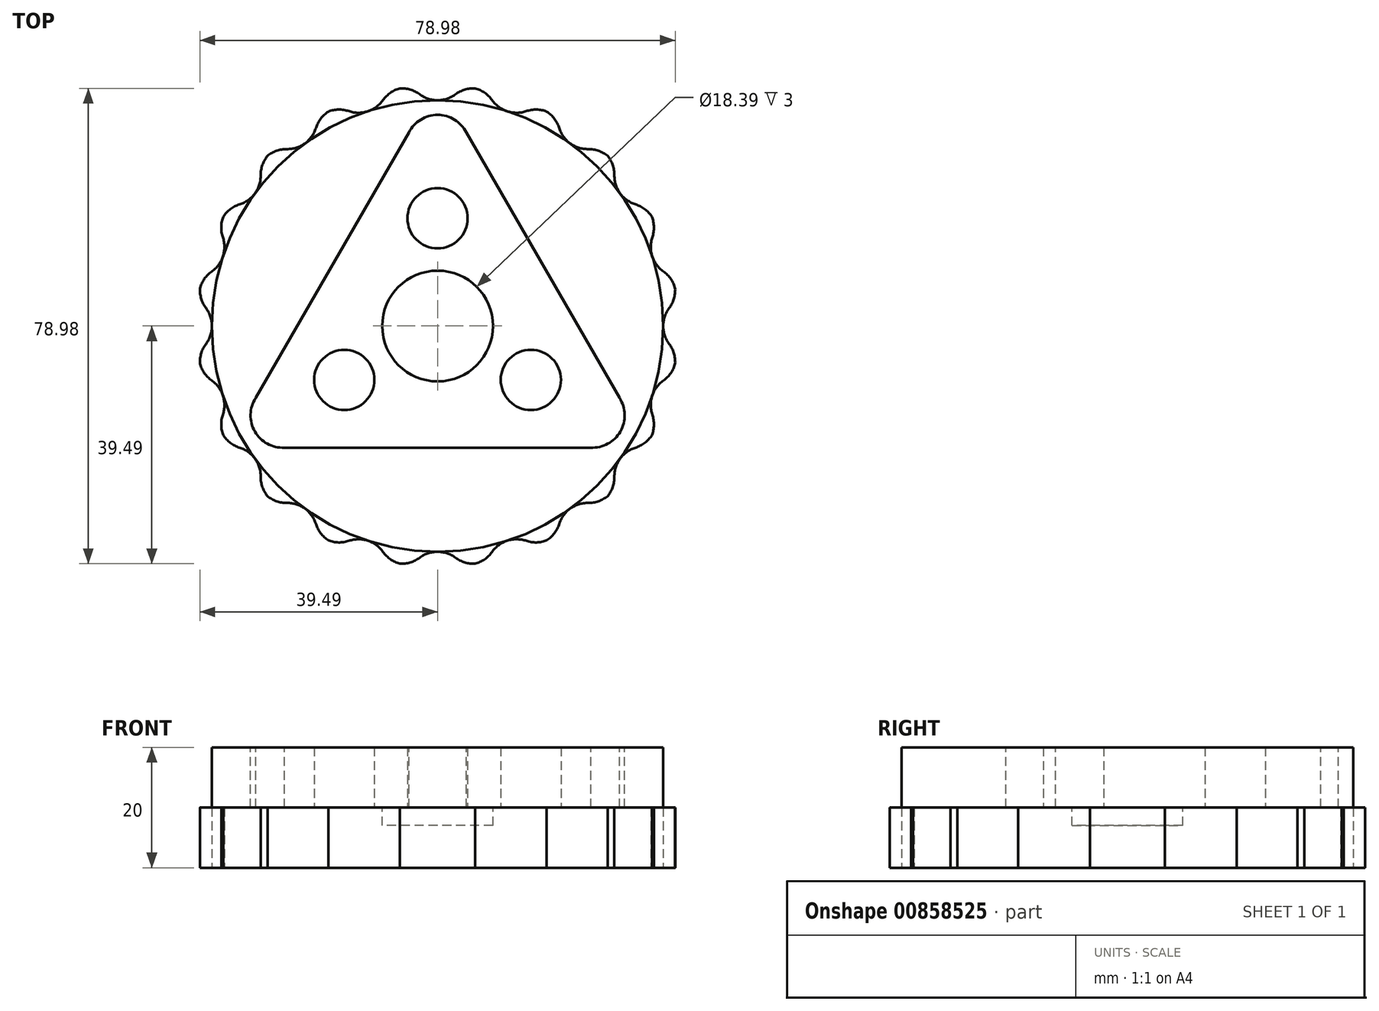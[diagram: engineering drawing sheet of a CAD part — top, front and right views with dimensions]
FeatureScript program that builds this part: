
annotation { "Feature Type Name" : "Feature", "Feature Type Description" : "" }
export const myFeature = defineFeature(function(context is Context, id is Id, definition is map)
    precondition{}
    {
        {
            var Q0;
            Q0=qCreatedBy(makeId("Top.planeOp"),FACE);
            var sketch = newSketch(context, id + "F0", { "sketchPlane" : qUnion([Q0])});
            skArc(sketch, "E0", {"start": v(-16.28, 36.54) * mm, "mid": v(-18.16, 35.64) * mm, "end": v(-19.99, 34.65) * mm});
            skCircle(sketch, "E1", {"center": v(0, 0) * mm, "radius": 42.5 * mm, "construction": true});
            skArc(sketch, "E2", {"start": v(-4.2, 39.78) * mm, "mid": v(0, 37.5) * mm, "end": v(4.2, 39.78) * mm});
            skArc(sketch, "E3.1.0", {"start": v(-16.28, 36.54) * mm, "mid": v(-11.59, 35.66) * mm, "end": v(-8.3, 39.13) * mm});
            skArc(sketch, "E3.2.0", {"start": v(-26.78, 29.72) * mm, "mid": v(-22.04, 30.34) * mm, "end": v(-19.99, 34.65) * mm});
            skArc(sketch, "E4.2.3.0", {"start": v(-34.65, 19.99) * mm, "mid": v(-30.34, 22.04) * mm, "end": v(-29.72, 26.78) * mm});
            skArc(sketch, "E4.2.4.0", {"start": v(-39.13, 8.3) * mm, "mid": v(-35.66, 11.59) * mm, "end": v(-36.54, 16.28) * mm});
            skArc(sketch, "E4.2.5.0", {"start": v(-39.78, -4.2) * mm, "mid": v(-37.5, 0) * mm, "end": v(-39.78, 4.2) * mm});
            skArc(sketch, "E4.2.6.0", {"start": v(-36.54, -16.28) * mm, "mid": v(-35.66, -11.59) * mm, "end": v(-39.13, -8.3) * mm});
            skArc(sketch, "E4.2.7.0", {"start": v(-29.72, -26.78) * mm, "mid": v(-30.34, -22.04) * mm, "end": v(-34.65, -19.99) * mm});
            skArc(sketch, "E4.2.8.0", {"start": v(-19.99, -34.65) * mm, "mid": v(-22.04, -30.34) * mm, "end": v(-26.78, -29.72) * mm});
            skArc(sketch, "E4.2.9.0", {"start": v(-8.3, -39.13) * mm, "mid": v(-11.59, -35.66) * mm, "end": v(-16.28, -36.54) * mm});
            skArc(sketch, "E5.2.10.0", {"start": v(4.2, -39.78) * mm, "mid": v(0, -37.5) * mm, "end": v(-4.2, -39.78) * mm});
            skArc(sketch, "E5.2.11.0", {"start": v(16.28, -36.54) * mm, "mid": v(11.59, -35.66) * mm, "end": v(8.3, -39.13) * mm});
            skArc(sketch, "E5.2.12.0", {"start": v(26.78, -29.72) * mm, "mid": v(22.04, -30.34) * mm, "end": v(19.99, -34.65) * mm});
            skArc(sketch, "E5.2.13.0", {"start": v(34.65, -19.99) * mm, "mid": v(30.34, -22.04) * mm, "end": v(29.72, -26.78) * mm});
            skArc(sketch, "E5.2.14.0", {"start": v(39.13, -8.3) * mm, "mid": v(35.66, -11.59) * mm, "end": v(36.54, -16.28) * mm});
            skArc(sketch, "E5.2.15.0", {"start": v(39.78, 4.2) * mm, "mid": v(37.5, 0) * mm, "end": v(39.78, -4.2) * mm});
            skArc(sketch, "E5.2.16.0", {"start": v(36.54, 16.28) * mm, "mid": v(35.66, 11.59) * mm, "end": v(39.13, 8.3) * mm});
            skArc(sketch, "E5.2.17.0", {"start": v(29.72, 26.78) * mm, "mid": v(30.34, 22.04) * mm, "end": v(34.65, 19.99) * mm});
            skArc(sketch, "E5.2.18.0", {"start": v(19.99, 34.65) * mm, "mid": v(22.04, 30.34) * mm, "end": v(26.78, 29.72) * mm});
            skArc(sketch, "E5.2.19.0", {"start": v(8.3, 39.13) * mm, "mid": v(11.59, 35.66) * mm, "end": v(16.28, 36.54) * mm});
            skArc(sketch, "E6.trimOffspring", {"start": v(-26.78, 29.72) * mm, "mid": v(-28.28, 28.28) * mm, "end": v(-29.72, 26.78) * mm});
            skArc(sketch, "E7.trimOffspring", {"start": v(-34.65, 19.99) * mm, "mid": v(-35.64, 18.16) * mm, "end": v(-36.54, 16.28) * mm});
            skArc(sketch, "E8.trimOffspring", {"start": v(-39.13, 8.3) * mm, "mid": v(-39.5, 6.26) * mm, "end": v(-39.78, 4.2) * mm});
            skArc(sketch, "E9.trimOffspring", {"start": v(-39.78, -4.2) * mm, "mid": v(-39.5, -6.26) * mm, "end": v(-39.13, -8.3) * mm});
            skArc(sketch, "E10.trimOffspring", {"start": v(-36.54, -16.28) * mm, "mid": v(-35.64, -18.16) * mm, "end": v(-34.65, -19.99) * mm});
            skArc(sketch, "E11.trimOffspring", {"start": v(-29.72, -26.78) * mm, "mid": v(-28.28, -28.28) * mm, "end": v(-26.78, -29.72) * mm});
            skArc(sketch, "E12.trimOffspring", {"start": v(-19.99, -34.65) * mm, "mid": v(-18.16, -35.64) * mm, "end": v(-16.28, -36.54) * mm});
            skArc(sketch, "E13.trimOffspring", {"start": v(-8.3, -39.13) * mm, "mid": v(-6.26, -39.5) * mm, "end": v(-4.2, -39.78) * mm});
            skArc(sketch, "E14.trimOffspring", {"start": v(4.2, -39.78) * mm, "mid": v(6.26, -39.5) * mm, "end": v(8.3, -39.13) * mm});
            skArc(sketch, "E15.trimOffspring", {"start": v(16.28, -36.54) * mm, "mid": v(18.16, -35.64) * mm, "end": v(19.99, -34.65) * mm});
            skArc(sketch, "E16.trimOffspring", {"start": v(26.78, -29.72) * mm, "mid": v(28.28, -28.28) * mm, "end": v(29.72, -26.78) * mm});
            skArc(sketch, "E17.trimOffspring", {"start": v(34.65, -19.99) * mm, "mid": v(35.64, -18.16) * mm, "end": v(36.54, -16.28) * mm});
            skArc(sketch, "E18.trimOffspring", {"start": v(39.13, -8.3) * mm, "mid": v(39.5, -6.26) * mm, "end": v(39.78, -4.2) * mm});
            skArc(sketch, "E19.trimOffspring", {"start": v(39.78, 4.2) * mm, "mid": v(39.5, 6.26) * mm, "end": v(39.13, 8.3) * mm});
            skArc(sketch, "E20.trimOffspring", {"start": v(36.54, 16.28) * mm, "mid": v(35.64, 18.16) * mm, "end": v(34.65, 19.99) * mm});
            skArc(sketch, "E21.trimOffspring", {"start": v(29.72, 26.78) * mm, "mid": v(28.28, 28.28) * mm, "end": v(26.78, 29.72) * mm});
            skArc(sketch, "E22.trimOffspring", {"start": v(19.99, 34.65) * mm, "mid": v(18.16, 35.64) * mm, "end": v(16.28, 36.54) * mm});
            skArc(sketch, "E23.trimOffspring", {"start": v(8.3, 39.13) * mm, "mid": v(6.26, 39.5) * mm, "end": v(4.2, 39.78) * mm});
            skArc(sketch, "E24.trimOffspring", {"start": v(-4.2, 39.78) * mm, "mid": v(-6.26, 39.5) * mm, "end": v(-8.3, 39.13) * mm});
            skSolve(sketch);
        }
        {
            var Q0;
            Q0 = qSketchRegion(id + "F0", true);
            extrude(context, id + "F1", {"entities" : qUnion([Q0]), "depth" : 10 * mm, "offsetDistance" : 25 * mm});
        }
        {
            var Q0;
            Q0=makeQuery(id+"F1.opExtrude","CAP_FACE",FACE,{"disambiguationData":[OSD([sQuery(id+"F0.wireOp",EDGE,"E0"),sQuery(id+"F0.wireOp",EDGE,"E2"),sQuery(id+"F0.wireOp",EDGE,"E3.1.0"),sQuery(id+"F0.wireOp",EDGE,"E3.2.0"),sQuery(id+"F0.wireOp",EDGE,"E4.2.3.0"),sQuery(id+"F0.wireOp",EDGE,"E4.2.4.0"),sQuery(id+"F0.wireOp",EDGE,"E4.2.5.0"),sQuery(id+"F0.wireOp",EDGE,"E4.2.6.0"),sQuery(id+"F0.wireOp",EDGE,"E4.2.7.0"),sQuery(id+"F0.wireOp",EDGE,"E4.2.8.0"),sQuery(id+"F0.wireOp",EDGE,"E4.2.9.0"),sQuery(id+"F0.wireOp",EDGE,"E5.2.10.0"),sQuery(id+"F0.wireOp",EDGE,"E5.2.11.0"),sQuery(id+"F0.wireOp",EDGE,"E5.2.12.0"),sQuery(id+"F0.wireOp",EDGE,"E5.2.13.0"),sQuery(id+"F0.wireOp",EDGE,"E5.2.14.0"),sQuery(id+"F0.wireOp",EDGE,"E5.2.15.0"),sQuery(id+"F0.wireOp",EDGE,"E5.2.16.0"),sQuery(id+"F0.wireOp",EDGE,"E5.2.17.0"),sQuery(id+"F0.wireOp",EDGE,"E5.2.18.0"),sQuery(id+"F0.wireOp",EDGE,"E5.2.19.0"),sQuery(id+"F0.wireOp",EDGE,"E6.trimOffspring"),sQuery(id+"F0.wireOp",EDGE,"E7.trimOffspring"),sQuery(id+"F0.wireOp",EDGE,"E8.trimOffspring"),sQuery(id+"F0.wireOp",EDGE,"E9.trimOffspring"),sQuery(id+"F0.wireOp",EDGE,"E10.trimOffspring"),sQuery(id+"F0.wireOp",EDGE,"E11.trimOffspring"),sQuery(id+"F0.wireOp",EDGE,"E12.trimOffspring"),sQuery(id+"F0.wireOp",EDGE,"E13.trimOffspring"),sQuery(id+"F0.wireOp",EDGE,"E14.trimOffspring"),sQuery(id+"F0.wireOp",EDGE,"E15.trimOffspring"),sQuery(id+"F0.wireOp",EDGE,"E16.trimOffspring"),sQuery(id+"F0.wireOp",EDGE,"E17.trimOffspring"),sQuery(id+"F0.wireOp",EDGE,"E18.trimOffspring"),sQuery(id+"F0.wireOp",EDGE,"E19.trimOffspring"),sQuery(id+"F0.wireOp",EDGE,"E20.trimOffspring"),sQuery(id+"F0.wireOp",EDGE,"E21.trimOffspring"),sQuery(id+"F0.wireOp",EDGE,"E22.trimOffspring"),sQuery(id+"F0.wireOp",EDGE,"E23.trimOffspring"),sQuery(id+"F0.wireOp",EDGE,"E24.trimOffspring")])],"isStart":false});
            var sketch = newSketch(context, id + "F2", { "sketchPlane" : qUnion([Q0])});
            skCircle(sketch, "E25", {"center": v(0, 0) * mm, "radius": 37.5 * mm});
            skSolve(sketch);
        }
        {
            var Q0;
            Q0 = qSketchRegion(id + "F2", true);
            extrude(context, id + "F3", {"entities" : qUnion([Q0]), "operationType" : NewBodyOperationType.ADD, "depth" : 10 * mm, "offsetDistance" : 25 * mm});
        }
        {
            var Q0;
            Q0=makeQuery(id+"F3.opExtrude","CAP_FACE",FACE,{"disambiguationData":[OSD([sQuery(id+"F2.wireOp",EDGE,"E25")])],"isStart":false});
            var sketch = newSketch(context, id + "F4", { "sketchPlane" : qUnion([Q0])});
            skCircle(sketch, "E26.cCircle", {"center": v(0, 0) * mm, "radius": 40.41 * mm, "construction": true});
            skLineSegment(sketch, "E26.0", {"start": v(4.5, 32.6) * mm, "end": v(30.5, -12.4) * mm});
            skLineSegment(sketch, "E26.1", {"start": v(25.98, -20.2) * mm, "end": v(-25.98, -20.2) * mm});
            skLineSegment(sketch, "E26.2", {"start": v(-30.5, -12.4) * mm, "end": v(-4.5, 32.6) * mm});
            skCircle(sketch, "E27.cCircle", {"center": v(0, 0) * mm, "radius": 17.9 * mm, "construction": true});
            skLineSegment(sketch, "E27.0", {"start": v(0, 17.9) * mm, "end": v(15.5, -8.95) * mm, "construction": true});
            skLineSegment(sketch, "E27.1", {"start": v(15.5, -8.95) * mm, "end": v(-15.5, -8.95) * mm, "construction": true});
            skLineSegment(sketch, "E27.2", {"start": v(-15.5, -8.95) * mm, "end": v(0, 17.9) * mm, "construction": true});
            skCircle(sketch, "E28", {"center": v(15.5, -8.95) * mm, "radius": 5 * mm, "construction": true});
            skCircle(sketch, "E29", {"center": v(0, 17.9) * mm, "radius": 5 * mm, "construction": true});
            skCircle(sketch, "E30", {"center": v(-15.5, -8.95) * mm, "radius": 5 * mm, "construction": true});
            skCircle(sketch, "E31", {"center": v(0, 0) * mm, "radius": 32.5 * mm, "construction": true});
            skPoint(sketch, "E32.first.point", {"position": v(-4.77, 32.15) * mm});
            skPoint(sketch, "E32.second.point", {"position": v(4.77, 32.15) * mm});
            skPoint(sketch, "E32.third.point", {"position": v(0, 34.27) * mm});
            skArc(sketch, "E33", {"start": v(4.77, 32.15) * mm, "mid": v(0, 35.06) * mm, "end": v(-4.77, 32.15) * mm});
            skPoint(sketch, "E33.third.point", {"position": v(0, 35.06) * mm});
            skArc(sketch, "E34.1.0", {"start": v(-30.23, -11.94) * mm, "mid": v(-30.36, -17.53) * mm, "end": v(-25.45, -20.2) * mm});
            skArc(sketch, "E34.2.0", {"start": v(25.45, -20.2) * mm, "mid": v(30.36, -17.53) * mm, "end": v(30.23, -11.94) * mm});
            skPoint(sketch, "E35.orphan", {"position": v(0, 40.41) * mm});
            skPoint(sketch, "E36.orphan", {"position": v(35, -20.2) * mm});
            skPoint(sketch, "E37.orphan", {"position": v(-35, -20.2) * mm});
            skSolve(sketch);
        }
        {
            var Q0;
            Q0 = qSketchRegion(id + "F4", true);
            extrude(context, id + "F5", {"entities" : qUnion([Q0]), "operationType" : NewBodyOperationType.REMOVE, "oppositeDirection" : true, "depth" : 10 * mm, "offsetDistance" : 25 * mm});
        }
        {
            var Q0;
            Q0=makeQuery(id+"F5.boolean.opBoolean","COPY",FACE,{"derivedFrom":makeQuery(id+"F5.opExtrude","CAP_FACE",FACE,{"disambiguationData":[OSD([sQuery(id+"F4.wireOp",EDGE,"E26.0"),sQuery(id+"F4.wireOp",EDGE,"E26.1"),sQuery(id+"F4.wireOp",EDGE,"E26.2"),sQuery(id+"F4.wireOp",EDGE,"E33"),sQuery(id+"F4.wireOp",EDGE,"E34.1.0"),sQuery(id+"F4.wireOp",EDGE,"E34.2.0")])],"isStart":false})});
            var sketch = newSketch(context, id + "F6", { "sketchPlane" : qUnion([Q0])});
            skCircle(sketch, "E38.cCircle", {"center": v(0, 0) * mm, "radius": 17.9 * mm, "construction": true});
            skLineSegment(sketch, "E38.0", {"start": v(0, 17.9) * mm, "end": v(15.5, -8.95) * mm, "construction": true});
            skLineSegment(sketch, "E38.1", {"start": v(15.5, -8.95) * mm, "end": v(-15.5, -8.95) * mm, "construction": true});
            skLineSegment(sketch, "E38.2", {"start": v(-15.5, -8.95) * mm, "end": v(0, 17.9) * mm, "construction": true});
            skCircle(sketch, "E39", {"center": v(0, 17.9) * mm, "radius": 5 * mm});
            skCircle(sketch, "E40", {"center": v(-15.5, -8.95) * mm, "radius": 5 * mm});
            skCircle(sketch, "E41", {"center": v(15.5, -8.95) * mm, "radius": 5 * mm});
            skSolve(sketch);
        }
        {
            var Q0;
            Q0 = qSketchRegion(id + "F6", true);
            extrude(context, id + "F7", {"entities" : qUnion([Q0]), "operationType" : NewBodyOperationType.ADD, "depth" : 10 * mm, "offsetDistance" : 25 * mm});
        }
        {
            var Q0;
            Q0=makeQuery(id+"F5.boolean.opBoolean","COPY",FACE,{"derivedFrom":makeQuery(id+"F5.opExtrude","CAP_FACE",FACE,{"disambiguationData":[OSD([sQuery(id+"F4.wireOp",EDGE,"E26.0"),sQuery(id+"F4.wireOp",EDGE,"E26.1"),sQuery(id+"F4.wireOp",EDGE,"E26.2"),sQuery(id+"F4.wireOp",EDGE,"E33"),sQuery(id+"F4.wireOp",EDGE,"E34.1.0"),sQuery(id+"F4.wireOp",EDGE,"E34.2.0")])],"isStart":false})});
            var sketch = newSketch(context, id + "F8", { "sketchPlane" : qUnion([Q0])});
            skCircle(sketch, "E42", {"center": v(0, 0) * mm, "radius": 9.2 * mm});
            skSolve(sketch);
        }
        {
            var Q0;
            Q0 = qSketchRegion(id + "F8", true);
            extrude(context, id + "F9", {"entities" : qUnion([Q0]), "operationType" : NewBodyOperationType.REMOVE, "oppositeDirection" : true, "depth" : 3 * mm, "offsetDistance" : 25 * mm});
        }
        {
            var Q0;
            Q0=makeQuery(id+"F1.opExtrude","SWEPT_EDGE",EDGE,{"disambiguationData":[OSD([sQuery(id+"F0.wireOp",EDGE,"E5.2.10.0"),sQuery(id+"F0.wireOp",EDGE,"E13.trimOffspring")])]});
            var Q1;
            Q1=makeQuery(id+"F1.opExtrude","SWEPT_EDGE",EDGE,{"disambiguationData":[OSD([sQuery(id+"F0.wireOp",EDGE,"E4.2.9.0"),sQuery(id+"F0.wireOp",EDGE,"E13.trimOffspring")])]});
            var Q2;
            Q2=makeQuery(id+"F1.opExtrude","SWEPT_EDGE",EDGE,{"disambiguationData":[OSD([sQuery(id+"F0.wireOp",EDGE,"E5.2.10.0"),sQuery(id+"F0.wireOp",EDGE,"E14.trimOffspring")])]});
            var Q3;
            Q3=makeQuery(id+"F1.opExtrude","SWEPT_EDGE",EDGE,{"disambiguationData":[OSD([sQuery(id+"F0.wireOp",EDGE,"E5.2.11.0"),sQuery(id+"F0.wireOp",EDGE,"E14.trimOffspring")])]});
            var Q4;
            Q4=makeQuery(id+"F1.opExtrude","SWEPT_EDGE",EDGE,{"disambiguationData":[OSD([sQuery(id+"F0.wireOp",EDGE,"E5.2.11.0"),sQuery(id+"F0.wireOp",EDGE,"E15.trimOffspring")])]});
            var Q5;
            Q5=makeQuery(id+"F1.opExtrude","SWEPT_EDGE",EDGE,{"disambiguationData":[OSD([sQuery(id+"F0.wireOp",EDGE,"E5.2.12.0"),sQuery(id+"F0.wireOp",EDGE,"E15.trimOffspring")])]});
            var Q6;
            Q6=makeQuery(id+"F1.opExtrude","SWEPT_EDGE",EDGE,{"disambiguationData":[OSD([sQuery(id+"F0.wireOp",EDGE,"E5.2.12.0"),sQuery(id+"F0.wireOp",EDGE,"E16.trimOffspring")])]});
            var Q7;
            Q7=makeQuery(id+"F1.opExtrude","SWEPT_EDGE",EDGE,{"disambiguationData":[OSD([sQuery(id+"F0.wireOp",EDGE,"E5.2.13.0"),sQuery(id+"F0.wireOp",EDGE,"E16.trimOffspring")])]});
            var Q8;
            Q8=makeQuery(id+"F1.opExtrude","SWEPT_EDGE",EDGE,{"disambiguationData":[OSD([sQuery(id+"F0.wireOp",EDGE,"E5.2.13.0"),sQuery(id+"F0.wireOp",EDGE,"E17.trimOffspring")])]});
            var Q9;
            Q9=makeQuery(id+"F1.opExtrude","SWEPT_EDGE",EDGE,{"disambiguationData":[OSD([sQuery(id+"F0.wireOp",EDGE,"E5.2.14.0"),sQuery(id+"F0.wireOp",EDGE,"E17.trimOffspring")])]});
            var Q10;
            Q10=makeQuery(id+"F1.opExtrude","SWEPT_EDGE",EDGE,{"disambiguationData":[OSD([sQuery(id+"F0.wireOp",EDGE,"E5.2.14.0"),sQuery(id+"F0.wireOp",EDGE,"E18.trimOffspring")])]});
            var Q11;
            Q11=makeQuery(id+"F1.opExtrude","SWEPT_EDGE",EDGE,{"disambiguationData":[OSD([sQuery(id+"F0.wireOp",EDGE,"E5.2.15.0"),sQuery(id+"F0.wireOp",EDGE,"E18.trimOffspring")])]});
            var Q12;
            Q12=makeQuery(id+"F1.opExtrude","SWEPT_EDGE",EDGE,{"disambiguationData":[OSD([sQuery(id+"F0.wireOp",EDGE,"E5.2.15.0"),sQuery(id+"F0.wireOp",EDGE,"E19.trimOffspring")])]});
            var Q13;
            Q13=makeQuery(id+"F1.opExtrude","SWEPT_EDGE",EDGE,{"disambiguationData":[OSD([sQuery(id+"F0.wireOp",EDGE,"E5.2.16.0"),sQuery(id+"F0.wireOp",EDGE,"E19.trimOffspring")])]});
            var Q14;
            Q14=makeQuery(id+"F1.opExtrude","SWEPT_EDGE",EDGE,{"disambiguationData":[OSD([sQuery(id+"F0.wireOp",EDGE,"E5.2.16.0"),sQuery(id+"F0.wireOp",EDGE,"E20.trimOffspring")])]});
            var Q15;
            Q15=makeQuery(id+"F1.opExtrude","SWEPT_EDGE",EDGE,{"disambiguationData":[OSD([sQuery(id+"F0.wireOp",EDGE,"E5.2.17.0"),sQuery(id+"F0.wireOp",EDGE,"E21.trimOffspring")])]});
            var Q16;
            Q16=makeQuery(id+"F1.opExtrude","SWEPT_EDGE",EDGE,{"disambiguationData":[OSD([sQuery(id+"F0.wireOp",EDGE,"E5.2.18.0"),sQuery(id+"F0.wireOp",EDGE,"E21.trimOffspring")])]});
            var Q17;
            Q17=makeQuery(id+"F1.opExtrude","SWEPT_EDGE",EDGE,{"disambiguationData":[OSD([sQuery(id+"F0.wireOp",EDGE,"E5.2.17.0"),sQuery(id+"F0.wireOp",EDGE,"E20.trimOffspring")])]});
            var Q18;
            Q18=makeQuery(id+"F1.opExtrude","SWEPT_EDGE",EDGE,{"disambiguationData":[OSD([sQuery(id+"F0.wireOp",EDGE,"E5.2.18.0"),sQuery(id+"F0.wireOp",EDGE,"E22.trimOffspring")])]});
            var Q19;
            Q19=makeQuery(id+"F1.opExtrude","SWEPT_EDGE",EDGE,{"disambiguationData":[OSD([sQuery(id+"F0.wireOp",EDGE,"E5.2.19.0"),sQuery(id+"F0.wireOp",EDGE,"E22.trimOffspring")])]});
            var Q20;
            Q20=makeQuery(id+"F1.opExtrude","SWEPT_EDGE",EDGE,{"disambiguationData":[OSD([sQuery(id+"F0.wireOp",EDGE,"E2"),sQuery(id+"F0.wireOp",EDGE,"E23.trimOffspring")])]});
            var Q21;
            Q21=makeQuery(id+"F1.opExtrude","SWEPT_EDGE",EDGE,{"disambiguationData":[OSD([sQuery(id+"F0.wireOp",EDGE,"E5.2.19.0"),sQuery(id+"F0.wireOp",EDGE,"E23.trimOffspring")])]});
            var Q22;
            Q22=makeQuery(id+"F1.opExtrude","SWEPT_EDGE",EDGE,{"disambiguationData":[OSD([sQuery(id+"F0.wireOp",EDGE,"E4.2.9.0"),sQuery(id+"F0.wireOp",EDGE,"E12.trimOffspring")])]});
            var Q23;
            Q23=makeQuery(id+"F1.opExtrude","SWEPT_EDGE",EDGE,{"disambiguationData":[OSD([sQuery(id+"F0.wireOp",EDGE,"E4.2.8.0"),sQuery(id+"F0.wireOp",EDGE,"E12.trimOffspring")])]});
            var Q24;
            Q24=makeQuery(id+"F1.opExtrude","SWEPT_EDGE",EDGE,{"disambiguationData":[OSD([sQuery(id+"F0.wireOp",EDGE,"E4.2.8.0"),sQuery(id+"F0.wireOp",EDGE,"E11.trimOffspring")])]});
            var Q25;
            Q25=makeQuery(id+"F1.opExtrude","SWEPT_EDGE",EDGE,{"disambiguationData":[OSD([sQuery(id+"F0.wireOp",EDGE,"E4.2.7.0"),sQuery(id+"F0.wireOp",EDGE,"E11.trimOffspring")])]});
            var Q26;
            Q26=makeQuery(id+"F1.opExtrude","SWEPT_EDGE",EDGE,{"disambiguationData":[OSD([sQuery(id+"F0.wireOp",EDGE,"E4.2.7.0"),sQuery(id+"F0.wireOp",EDGE,"E10.trimOffspring")])]});
            var Q27;
            Q27=makeQuery(id+"F1.opExtrude","SWEPT_EDGE",EDGE,{"disambiguationData":[OSD([sQuery(id+"F0.wireOp",EDGE,"E4.2.6.0"),sQuery(id+"F0.wireOp",EDGE,"E10.trimOffspring")])]});
            var Q28;
            Q28=makeQuery(id+"F1.opExtrude","SWEPT_EDGE",EDGE,{"disambiguationData":[OSD([sQuery(id+"F0.wireOp",EDGE,"E4.2.6.0"),sQuery(id+"F0.wireOp",EDGE,"E9.trimOffspring")])]});
            var Q29;
            Q29=makeQuery(id+"F1.opExtrude","SWEPT_EDGE",EDGE,{"disambiguationData":[OSD([sQuery(id+"F0.wireOp",EDGE,"E4.2.5.0"),sQuery(id+"F0.wireOp",EDGE,"E9.trimOffspring")])]});
            var Q30;
            Q30=makeQuery(id+"F1.opExtrude","SWEPT_EDGE",EDGE,{"disambiguationData":[OSD([sQuery(id+"F0.wireOp",EDGE,"E4.2.5.0"),sQuery(id+"F0.wireOp",EDGE,"E8.trimOffspring")])]});
            var Q31;
            Q31=makeQuery(id+"F1.opExtrude","SWEPT_EDGE",EDGE,{"disambiguationData":[OSD([sQuery(id+"F0.wireOp",EDGE,"E4.2.4.0"),sQuery(id+"F0.wireOp",EDGE,"E8.trimOffspring")])]});
            var Q32;
            Q32=makeQuery(id+"F1.opExtrude","SWEPT_EDGE",EDGE,{"disambiguationData":[OSD([sQuery(id+"F0.wireOp",EDGE,"E4.2.4.0"),sQuery(id+"F0.wireOp",EDGE,"E7.trimOffspring")])]});
            var Q33;
            Q33=makeQuery(id+"F1.opExtrude","SWEPT_EDGE",EDGE,{"disambiguationData":[OSD([sQuery(id+"F0.wireOp",EDGE,"E4.2.3.0"),sQuery(id+"F0.wireOp",EDGE,"E7.trimOffspring")])]});
            var Q34;
            Q34=makeQuery(id+"F1.opExtrude","SWEPT_EDGE",EDGE,{"disambiguationData":[OSD([sQuery(id+"F0.wireOp",EDGE,"E4.2.3.0"),sQuery(id+"F0.wireOp",EDGE,"E6.trimOffspring")])]});
            var Q35;
            Q35=makeQuery(id+"F1.opExtrude","SWEPT_EDGE",EDGE,{"disambiguationData":[OSD([sQuery(id+"F0.wireOp",EDGE,"E3.2.0"),sQuery(id+"F0.wireOp",EDGE,"E6.trimOffspring")])]});
            var Q36;
            Q36=makeQuery(id+"F1.opExtrude","SWEPT_EDGE",EDGE,{"disambiguationData":[OSD([sQuery(id+"F0.wireOp",EDGE,"E0"),sQuery(id+"F0.wireOp",EDGE,"E3.2.0")])]});
            var Q37;
            Q37=makeQuery(id+"F1.opExtrude","SWEPT_EDGE",EDGE,{"disambiguationData":[OSD([sQuery(id+"F0.wireOp",EDGE,"E0"),sQuery(id+"F0.wireOp",EDGE,"E3.1.0")])]});
            var Q38;
            Q38=makeQuery(id+"F1.opExtrude","SWEPT_EDGE",EDGE,{"disambiguationData":[OSD([sQuery(id+"F0.wireOp",EDGE,"E3.1.0"),sQuery(id+"F0.wireOp",EDGE,"E24.trimOffspring")])]});
            var Q39;
            Q39=makeQuery(id+"F1.opExtrude","SWEPT_EDGE",EDGE,{"disambiguationData":[OSD([sQuery(id+"F0.wireOp",EDGE,"E2"),sQuery(id+"F0.wireOp",EDGE,"E24.trimOffspring")])]});
            fillet(context, id + "F10", {"entities" : qUnion([Q0, Q1, Q2, Q3, Q4, Q5, Q6, Q7, Q8, Q9, Q10, Q11, Q12, Q13, Q14, Q15, Q16, Q17, Q18, Q19, Q20, Q21, Q22, Q23, Q24, Q25, Q26, Q27, Q28, Q29, Q30, Q31, Q32, Q33, Q34, Q35, Q36, Q37, Q38, Q39]), "radius" : 5 * mm, "tangentPropagation" : true, "allowEdgeOverflow" : false});
        }
    });
